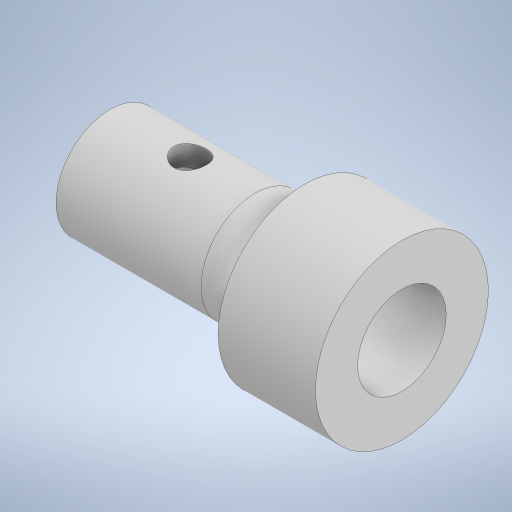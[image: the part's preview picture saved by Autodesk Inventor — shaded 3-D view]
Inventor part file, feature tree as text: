
AUTODESK INVENTOR PART (.ipt)
format: ipt  version: 2024 (Build 280153000, 153)  size: 272,384 bytes
history: native  units: in
note: dims shown in document units (in); Inventor stores cm internally (conversion verified against a paired STEP export)
features: extrude x4, sketch x4, fillet x1
ambient origin geometry x8: Origin, YZ Plane, XZ Plane, XY Plane, X Axis, Y Axis, Z Axis, Center Point
bodies: Solid1 (feature_tree)
feature tree (9):
  extrude  "Extrusion1"  Depth=0.3937in
  extrude  "Extrusion2"  Depth=0.3937in
  extrude  "Extrusion3"  Depth=0.3228in
  fillet  "Fillet1"  Radius=0.6299in
  extrude  "Extrusion4"  Depth=0.1969in
  sketch  "Sketch1"  dims[d0=0.248in d1=0.3937in]
  sketch  "Sketch2"  dims[d2=0.7087in d3=0.0in d4=0.3937in]
  sketch  "Sketch3"  dims[d5=0.0787in d6=0.0in d7=0.3228in d8=0.6299in]
  sketch  "Sketch4"  dims[d9=0.3543in d10=0.0in d11=0.1969in d12=0.2362in d13=0.1181in d14=1.7323in d15=0.0in]
